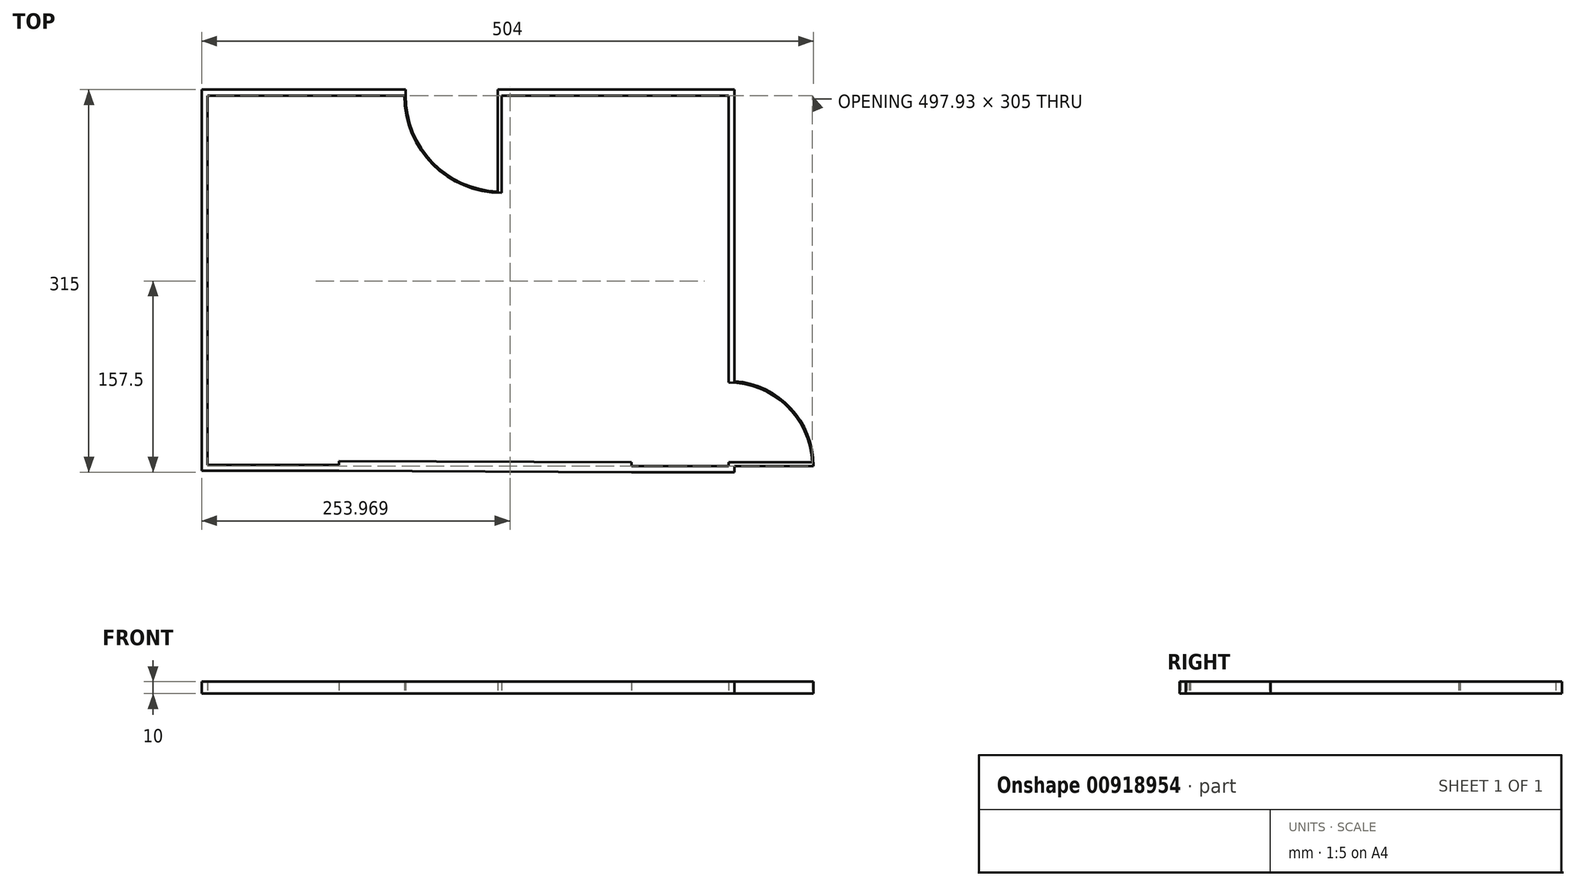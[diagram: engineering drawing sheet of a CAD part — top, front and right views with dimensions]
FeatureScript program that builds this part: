
annotation { "Feature Type Name" : "Feature", "Feature Type Description" : "" }
export const myFeature = defineFeature(function(context is Context, id is Id, definition is map)
    precondition{}
    {
        {
            var Q0;
            Q0=qCreatedBy(makeId("Top.planeOp"),FACE);
            var sketch = newSketch(context, id + "F0", { "sketchPlane" : qUnion([Q0])});
            skLineSegment(sketch, "E0", {"start": v(-193.68, 152.24) * mm, "end": v(-31.68, 152.24) * mm});
            skLineSegment(sketch, "E1", {"start": v(48.32, 152.24) * mm, "end": v(235.32, 152.24) * mm});
            skLineSegment(sketch, "E2", {"start": v(235.32, 152.24) * mm, "end": v(235.32, -82.76) * mm});
            skLineSegment(sketch, "E3", {"start": v(235.32, -152.76) * mm, "end": v(155.32, -152.76) * mm});
            skLineSegment(sketch, "E4", {"start": v(-85.68, -151.76) * mm, "end": v(-193.68, -151.76) * mm});
            skLineSegment(sketch, "E5", {"start": v(-193.68, -151.76) * mm, "end": v(-193.68, 152.24) * mm});
            skArc(sketch, "E6", {"start": v(-31.68, 152.24) * mm, "mid": v(-8.25, 95.67) * mm, "end": v(48.32, 72.24) * mm});
            skLineSegment(sketch, "E7.0", {"start": v(-85.69, -156.76) * mm, "end": v(-198.68, -156.76) * mm});
            skLineSegment(sketch, "E7.1", {"start": v(155.31, -157.76) * mm, "end": v(-85.69, -156.76) * mm});
            skLineSegment(sketch, "E7.2", {"start": v(-198.68, -156.76) * mm, "end": v(-198.68, 157.24) * mm});
            skLineSegment(sketch, "E7.3", {"start": v(240.32, -157.76) * mm, "end": v(155.31, -157.76) * mm});
            skLineSegment(sketch, "E7.4", {"start": v(240.32, -152.76) * mm, "end": v(240.32, -157.76) * mm});
            skLineSegment(sketch, "E7.5", {"start": v(-198.68, 157.24) * mm, "end": v(-31.68, 157.24) * mm});
            skLineSegment(sketch, "E7.7", {"start": v(48.32, 157.24) * mm, "end": v(240.32, 157.24) * mm});
            skLineSegment(sketch, "E7.8", {"start": v(240.32, 157.24) * mm, "end": v(240.32, -82.76) * mm});
            skLineSegment(sketch, "E8", {"start": v(48.32, 152.24) * mm, "end": v(48.32, 157.24) * mm});
            skArc(sketch, "E9.0", {"start": v(-30.68, 152.24) * mm, "mid": v(-8.6, 97.45) * mm, "end": v(45.32, 73.3) * mm});
            skLineSegment(sketch, "E10", {"start": v(48.32, 73.24) * mm, "end": v(48.32, 72.24) * mm});
            skLineSegment(sketch, "E11", {"start": v(-30.68, 152.24) * mm, "end": v(-30.68, 157.24) * mm});
            skLineSegment(sketch, "E12", {"start": v(-30.68, 157.24) * mm, "end": v(-31.68, 157.24) * mm});
            skLineSegment(sketch, "E13", {"start": v(-85.68, -151.76) * mm, "end": v(-85.68, -148.76) * mm});
            skLineSegment(sketch, "E14", {"start": v(-85.68, -148.76) * mm, "end": v(155.32, -149.76) * mm});
            skLineSegment(sketch, "E15", {"start": v(155.32, -149.76) * mm, "end": v(155.32, -152.76) * mm});
            skArc(sketch, "E16", {"start": v(240.32, -82.94) * mm, "mid": v(286.56, -105.06) * mm, "end": v(305.32, -152.76) * mm});
            skArc(sketch, "E17.0", {"start": v(235.32, -83.76) * mm, "mid": v(283.04, -102.92) * mm, "end": v(304.26, -149.75) * mm});
            skLineSegment(sketch, "E18", {"start": v(235.32, -82.76) * mm, "end": v(235.32, -83.76) * mm});
            skLineSegment(sketch, "E19", {"start": v(304.32, -152.76) * mm, "end": v(305.32, -152.76) * mm});
            skLineSegment(sketch, "E20", {"start": v(240.32, -82.76) * mm, "end": v(240.32, -82.94) * mm});
            skLineSegment(sketch, "E21", {"start": v(48.32, 73.24) * mm, "end": v(48.32, 152.24) * mm});
            skLineSegment(sketch, "E22", {"start": v(48.32, 157.24) * mm, "end": v(45.32, 157.24) * mm});
            skLineSegment(sketch, "E23", {"start": v(45.32, 157.24) * mm, "end": v(45.32, 73.3) * mm});
            skLineSegment(sketch, "E24", {"start": v(240.32, -152.76) * mm, "end": v(304.32, -152.76) * mm});
            skLineSegment(sketch, "E25", {"start": v(235.32, -152.76) * mm, "end": v(235.32, -149.75) * mm});
            skLineSegment(sketch, "E26", {"start": v(235.32, -149.75) * mm, "end": v(304.26, -149.75) * mm});
            skSolve(sketch);
        }
        {
            var Q0;
            Q0=makeQuery(id+"F0.imprint","IMPRINT",FACE,{"disambiguationData":[TD([[makeQuery(id+"F0.imprint","IMPRINT",EDGE,{"derivedFrom":sQuery(id+"F0.wireOp",EDGE,"E0")}),1.0]])]});
            var Q1;
            Q1=makeQuery(id+"F0.imprint","IMPRINT",FACE,{"disambiguationData":[TD([[makeQuery(id+"F0.imprint","IMPRINT",EDGE,{"derivedFrom":sQuery(id+"F0.wireOp",EDGE,"E1")}),1.0]])]});
            extrude(context, id + "F1", {"entities" : qUnion([Q0, Q1]), "depth" : 10 * mm, "offsetDistance" : 25 * mm});
        }
    });
